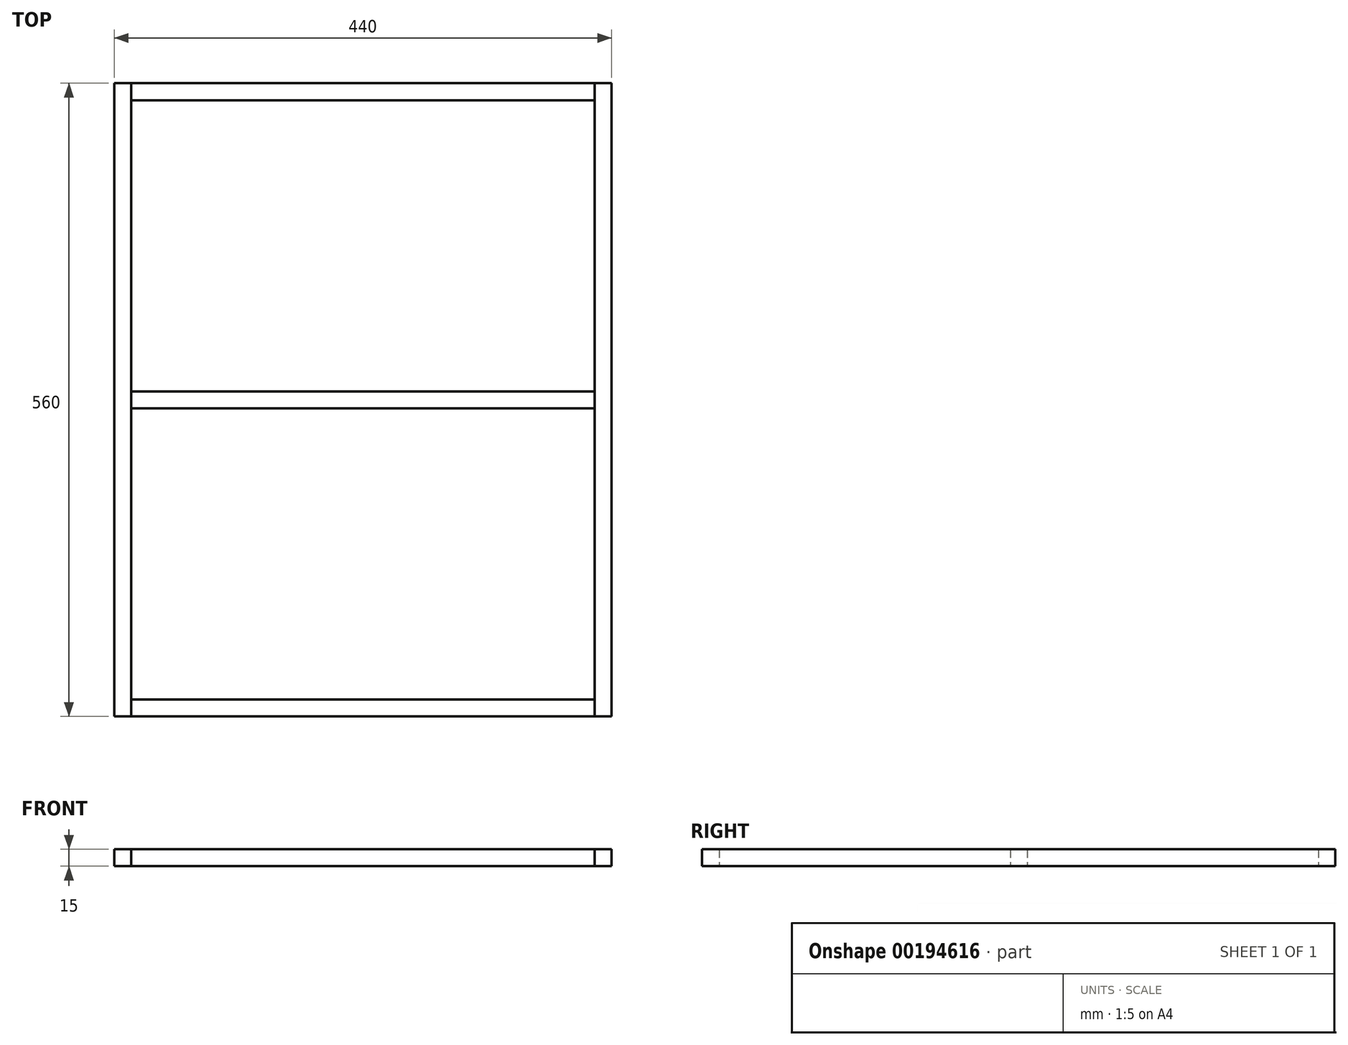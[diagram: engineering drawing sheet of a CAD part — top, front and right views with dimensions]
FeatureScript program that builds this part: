
annotation { "Feature Type Name" : "Feature", "Feature Type Description" : "" }
export const myFeature = defineFeature(function(context is Context, id is Id, definition is map)
    precondition{}
    {
        {
            var Q0;
            Q0=qCreatedBy(makeId("Top.planeOp"),FACE);
            var sketch = newSketch(context, id + "F0", { "sketchPlane" : qUnion([Q0])});
            skLineSegment(sketch, "E0.bottom", {"start": v(220, 280) * mm, "end": v(-220, 280) * mm});
            skLineSegment(sketch, "E0.top", {"start": v(220, -280) * mm, "end": v(-220, -280) * mm});
            skLineSegment(sketch, "E0.left", {"start": v(220, 280) * mm, "end": v(220, -280) * mm});
            skLineSegment(sketch, "E0.right", {"start": v(-220, 280) * mm, "end": v(-220, -280) * mm});
            skPoint(sketch, "E0.middle", {"position": v(0, 0) * mm});
            skLineSegment(sketch, "E1", {"start": v(-205, 280) * mm, "end": v(-205, -280) * mm});
            skLineSegment(sketch, "E2", {"start": v(205, 280) * mm, "end": v(205, -280) * mm});
            skLineSegment(sketch, "E3", {"start": v(-205, -265) * mm, "end": v(205, -265) * mm});
            skLineSegment(sketch, "E4", {"start": v(-205, 265) * mm, "end": v(205, 265) * mm});
            skLineSegment(sketch, "E5.bottom", {"start": v(205, 7.5) * mm, "end": v(-205, 7.5) * mm});
            skLineSegment(sketch, "E5.top", {"start": v(205, -7.5) * mm, "end": v(-205, -7.5) * mm});
            skLineSegment(sketch, "E5.left", {"start": v(205, 7.5) * mm, "end": v(205, -7.5) * mm});
            skLineSegment(sketch, "E5.right", {"start": v(-205, 7.5) * mm, "end": v(-205, -7.5) * mm});
            skSolve(sketch);
        }
        {
            var Q0;
            {var subQ5=sQuery(id+"F0.wireOp",EDGE,"E0.right");Q0=makeQuery(id+"F0.imprint","IMPRINT",FACE,{"disambiguationData":[TD([[makeQuery(id+"F0.imprint","IMPRINT",EDGE,{"derivedFrom":subQ5}),1.0]])]});}
            var Q1;
            {var subQ4=sQuery(id+"F0.wireOp",EDGE,"E0.left");Q1=makeQuery(id+"F0.imprint","IMPRINT",FACE,{"disambiguationData":[TD([[makeQuery(id+"F0.imprint","IMPRINT",EDGE,{"derivedFrom":subQ4}),-1.0]])]});}
            extrude(context, id + "F1", {"entities" : qUnion([Q0, Q1]), "depth" : 15 * mm});
        }
        {
            var Q0;
            {var subQ5=sQuery(id+"F0.wireOp",EDGE,"E4");Q0=makeQuery(id+"F0.imprint","IMPRINT",FACE,{"disambiguationData":[TD([[makeQuery(id+"F0.imprint","IMPRINT",EDGE,{"derivedFrom":subQ5}),1.0]])]});}
            var Q1;
            Q1=makeQuery(id+"F0.imprint","IMPRINT",FACE,{"disambiguationData":[TD([[makeQuery(id+"F0.imprint","IMPRINT",EDGE,{"derivedFrom":sQuery(id+"F0.wireOp",EDGE,"E5.bottom")}),1.0]])]});
            var Q2;
            {var subQ5=sQuery(id+"F0.wireOp",EDGE,"E3");Q2=makeQuery(id+"F0.imprint","IMPRINT",FACE,{"disambiguationData":[TD([[makeQuery(id+"F0.imprint","IMPRINT",EDGE,{"derivedFrom":subQ5}),-1.0]])]});}
            extrude(context, id + "F2", {"entities" : qUnion([Q0, Q1, Q2]), "depth" : 15 * mm});
        }
    });
